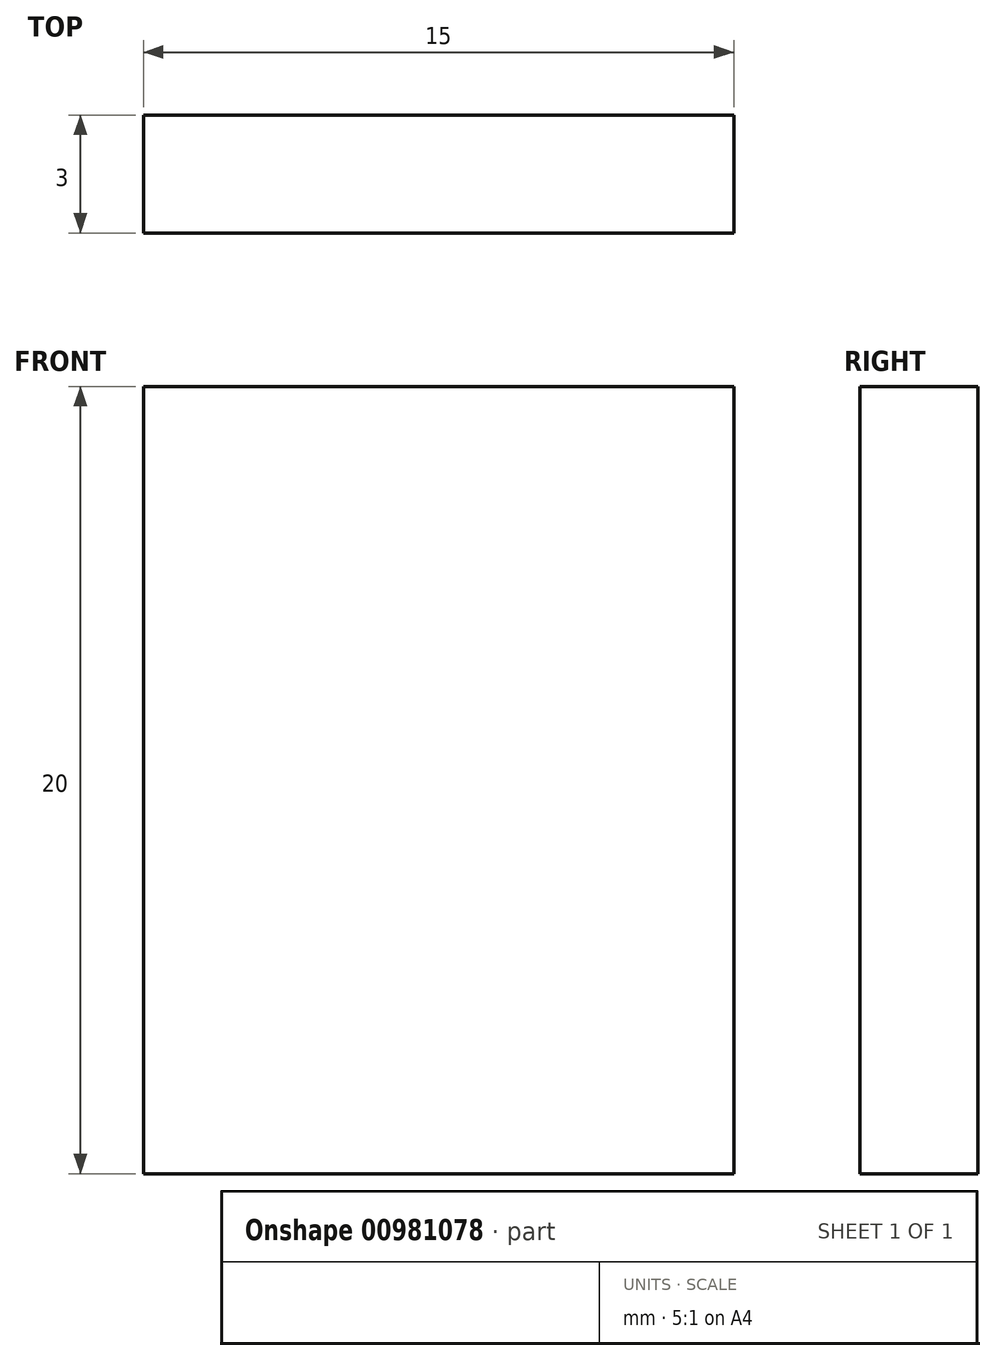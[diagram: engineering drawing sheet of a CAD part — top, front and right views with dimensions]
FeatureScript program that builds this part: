
annotation { "Feature Type Name" : "Feature", "Feature Type Description" : "" }
export const myFeature = defineFeature(function(context is Context, id is Id, definition is map)
    precondition{}
    {
        {
            var Q0;
            Q0=qCreatedBy(makeId("Top.planeOp"),FACE);
            var sketch = newSketch(context, id + "F0", { "sketchPlane" : qUnion([Q0])});
            skLineSegment(sketch, "E0.bottom", {"start": v(-7.5, 0) * mm, "end": v(7.5, 0) * mm});
            skLineSegment(sketch, "E0.top", {"start": v(-7.5, -3) * mm, "end": v(7.5, -3) * mm});
            skLineSegment(sketch, "E0.left", {"start": v(-7.5, 0) * mm, "end": v(-7.5, -3) * mm});
            skLineSegment(sketch, "E0.right", {"start": v(7.5, 0) * mm, "end": v(7.5, -3) * mm});
            skFitSpline(sketch, "E1", {"points": [v(7.5, 0) * mm, v(5.5, 10) * mm, v(0, 10) * mm, v(-7.5, 2.94) * mm], "startDerivative": vector(0.98, 41.77) * mm, "endDerivative": vector(-38.66, -47.28) * mm});
            skFitSpline(sketch, "E2.0", {"points": [v(9.5, -0.05) * mm, v(9.52, 0.83) * mm, v(9.55, 2.53) * mm, v(9.5, 4.85) * mm, v(9.28, 6.95) * mm, v(8.9, 8.54) * mm, v(8.39, 9.73) * mm, v(7.86, 10.56) * mm, v(7.27, 11.19) * mm, v(6.72, 11.6) * mm, v(6.11, 11.97) * mm, v(5.34, 12.27) * mm, v(4.43, 12.46) * mm, v(3.53, 12.53) * mm, v(2.37, 12.5) * mm, v(1.28, 12.36) * mm, v(0.29, 12.15) * mm, v(-0.28, 12) * mm, v(-0.7, 11.88) * mm, v(-1.11, 11.75) * mm, v(-1.64, 11.57) * mm, v(-2.27, 11.28) * mm, v(-2.9, 10.9) * mm, v(-3.5, 10.46) * mm, v(-4.3, 9.76) * mm, v(-5.32, 8.68) * mm, v(-6.87, 6.87) * mm, v(-8.24, 5.19) * mm, v(-9.05, 4.2) * mm]});
            skLineSegment(sketch, "E3", {"start": v(7.5, -3) * mm, "end": v(9.5, -3) * mm});
            skLineSegment(sketch, "E4", {"start": v(9.5, -3) * mm, "end": v(9.5, -0.02) * mm});
            skLineSegment(sketch, "E5", {"start": v(-7.5, 6.1) * mm, "end": v(-7.5, 2.94) * mm});
            skLineSegment(sketch, "E6", {"start": v(0, 10) * mm, "end": v(5.5, 10) * mm, "construction": true});
            skSolve(sketch);
        }
        {
            var Q0;
            Q0=makeQuery(id+"F0.imprint","IMPRINT",FACE,{"disambiguationData":[TD([[makeQuery(id+"F0.imprint","IMPRINT",EDGE,{"derivedFrom":sQuery(id+"F0.wireOp",EDGE,"E0.right")}),1.0]])]});
            var Q1;
            Q1=makeQuery(id+"F0.imprint","IMPRINT",FACE,{"disambiguationData":[TD([[makeQuery(id+"F0.imprint","IMPRINT",EDGE,{"derivedFrom":sQuery(id+"F0.wireOp",EDGE,"E0.bottom")}),-1.0]])]});
            extrude(context, id + "F1", {"entities" : qUnion([Q0, Q1]), "depth" : 20 * mm, "offsetDistance" : 25 * mm});
        }
    });
